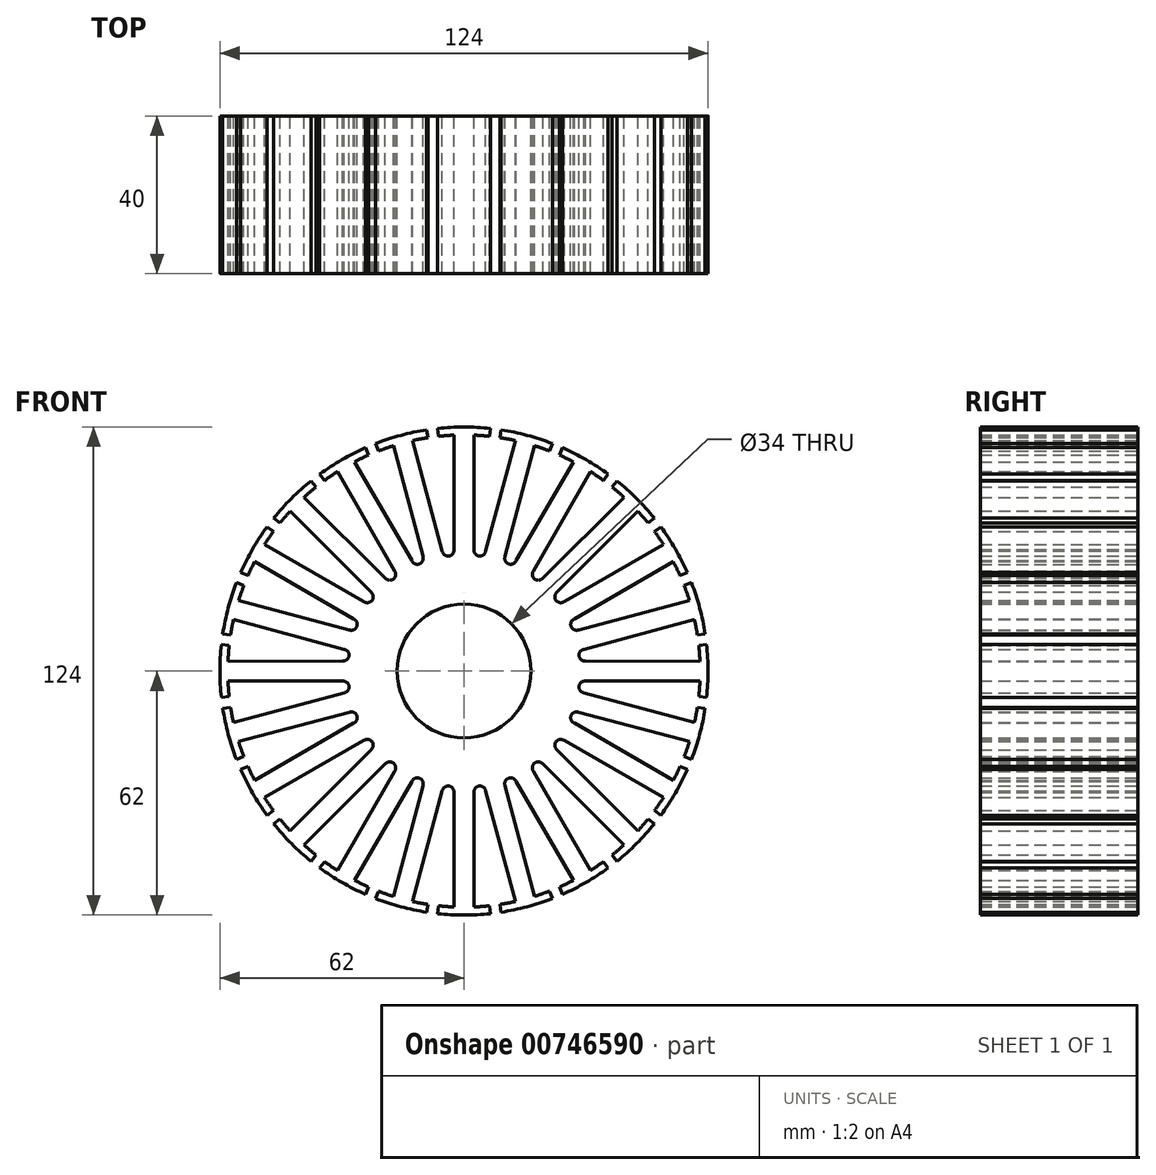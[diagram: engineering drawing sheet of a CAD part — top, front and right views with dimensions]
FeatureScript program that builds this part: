
annotation { "Feature Type Name" : "Feature", "Feature Type Description" : "" }
export const myFeature = defineFeature(function(context is Context, id is Id, definition is map)
    precondition{}
    {
        {
            var Q0;
            Q0=qCreatedBy(makeId("Front.planeOp"),FACE);
            var sketch = newSketch(context, id + "F0", { "sketchPlane" : qUnion([Q0])});
            skArc(sketch, "E0", {"start": v(6.72, 61.63) * mm, "mid": v(0, 62) * mm, "end": v(-6.72, 61.63) * mm});
            skArc(sketch, "E1", {"start": v(6.46, 59.65) * mm, "mid": v(4.48, 59.83) * mm, "end": v(2.5, 59.95) * mm});
            skCircle(sketch, "E2", {"center": v(0, 0) * mm, "radius": 17 * mm});
            skArc(sketch, "E3.trimOffspring", {"start": v(-9.2, 59.3) * mm, "mid": v(-11.16, 58.95) * mm, "end": v(-13.1, 58.55) * mm});
            skArc(sketch, "E4.trimOffspring", {"start": v(-9.46, 61.27) * mm, "mid": v(-16.05, 59.89) * mm, "end": v(-22.45, 57.8) * mm});
            skLineSegment(sketch, "E5.trimOffspring", {"start": v(6.46, 59.65) * mm, "end": v(6.72, 61.63) * mm});
            skLineSegment(sketch, "E6.trimOffspring", {"start": v(-6.46, 59.65) * mm, "end": v(-6.72, 61.63) * mm});
            skLineSegment(sketch, "E7.trimOffspring", {"start": v(-9.2, 59.3) * mm, "end": v(-9.46, 61.27) * mm});
            skLineSegment(sketch, "E8.MirrorCS", {"start": v(-21.68, 55.95) * mm, "end": v(-22.45, 57.8) * mm});
            skCircle(sketch, "E9", {"center": v(0, 0) * mm, "radius": 31 * mm, "construction": true});
            skArc(sketch, "E10", {"start": v(2.55, 30.9) * mm, "mid": v(3.85, 29.22) * mm, "end": v(5.53, 30.5) * mm});
            skArc(sketch, "E11.MirrorC", {"start": v(-2.55, 30.9) * mm, "mid": v(-3.85, 29.22) * mm, "end": v(-5.53, 30.5) * mm});
            skLineSegment(sketch, "E12.MirrorCS", {"start": v(-10.41, 29.2) * mm, "end": v(-17.93, 57.26) * mm});
            skArc(sketch, "E13.MirrorC", {"start": v(10.46, 29.18) * mm, "mid": v(11.28, 27.23) * mm, "end": v(13.24, 28.03) * mm});
            skLineSegment(sketch, "E14.trimOffspring", {"start": v(-5.58, 30.5) * mm, "end": v(-13.1, 58.55) * mm});
            skArc(sketch, "E15.MirrorCS", {"start": v(-13.24, 28.03) * mm, "mid": v(-11.28, 27.23) * mm, "end": v(-10.46, 29.18) * mm});
            skArc(sketch, "E16.trimOffspring", {"start": v(-2.5, 59.95) * mm, "mid": v(-4.48, 59.83) * mm, "end": v(-6.46, 59.65) * mm});
            skArc(sketch, "E17.trimOffspring", {"start": v(-17.93, 57.26) * mm, "mid": v(-19.82, 56.63) * mm, "end": v(-21.68, 55.95) * mm});
            skLineSegment(sketch, "E18", {"start": v(0, 0) * mm, "end": v(0, 29.47) * mm});
            skLineSegment(sketch, "E19", {"start": v(2.5, 59.95) * mm, "end": v(2.55, 30.9) * mm});
            skLineSegment(sketch, "E20", {"start": v(-2.55, 30.9) * mm, "end": v(-2.5, 59.95) * mm});
            skLineSegment(sketch, "E21.MirrorCS", {"start": v(13.1, 58.55) * mm, "end": v(5.53, 30.5) * mm});
            skLineSegment(sketch, "E22.MirrorCS", {"start": v(10.46, 29.18) * mm, "end": v(17.93, 57.26) * mm});
            skArc(sketch, "E23.MirrorCS", {"start": v(9.2, 59.3) * mm, "mid": v(11.16, 58.95) * mm, "end": v(13.1, 58.55) * mm});
            skArc(sketch, "E24.MirrorCS", {"start": v(17.93, 57.26) * mm, "mid": v(19.82, 56.63) * mm, "end": v(21.68, 55.95) * mm});
            skLineSegment(sketch, "E25.MirrorCS", {"start": v(9.2, 59.3) * mm, "end": v(9.46, 61.27) * mm});
            skLineSegment(sketch, "E26.MirrorCS", {"start": v(21.68, 55.95) * mm, "end": v(22.45, 57.8) * mm});
            skLineSegment(sketch, "E27", {"start": v(0, 0) * mm, "end": v(31, 0) * mm});
            skLineSegment(sketch, "E28.MirrorCS", {"start": v(59.76, -5.35) * mm, "end": v(30.96, -1.5) * mm});
            skLineSegment(sketch, "E29.MirrorCS", {"start": v(59.76, 5.35) * mm, "end": v(30.96, 1.5) * mm});
            skArc(sketch, "E30.MirrorCS", {"start": v(30.96, -1.5) * mm, "mid": v(29.47, 0) * mm, "end": v(30.96, 1.5) * mm});
            skLineSegment(sketch, "E31.MirrorCS", {"start": v(59.98, 1.38) * mm, "end": v(61.98, 1.38) * mm});
            skLineSegment(sketch, "E32.MirrorCS", {"start": v(59.98, -1.38) * mm, "end": v(61.98, -1.38) * mm});
            skArc(sketch, "E33.MirrorCS", {"start": v(59.98, -1.38) * mm, "mid": v(59.9, -3.36) * mm, "end": v(59.76, -5.35) * mm});
            skArc(sketch, "E34.MirrorCS", {"start": v(59.98, 1.38) * mm, "mid": v(59.9, 3.36) * mm, "end": v(59.76, 5.35) * mm});
            skArc(sketch, "E35.trimOffspring", {"start": v(22.45, 57.8) * mm, "mid": v(16.05, 59.89) * mm, "end": v(9.46, 61.27) * mm});
            skArc(sketch, "E36.trimOffspring", {"start": v(21.68, 55.95) * mm, "mid": v(19.82, 56.63) * mm, "end": v(17.93, 57.26) * mm});
            skLineSegment(sketch, "E37", {"start": v(3.85, 29.22) * mm, "end": v(0, 0) * mm});
            skLineSegment(sketch, "E38", {"start": v(-3.85, 29.22) * mm, "end": v(0, 0) * mm});
            skArc(sketch, "E39.trimOffspring", {"start": v(59.76, -5.35) * mm, "mid": v(59.9, -3.36) * mm, "end": v(59.98, -1.38) * mm});
            skCircle(sketch, "E40", {"center": v(0, 0) * mm, "radius": 29.47 * mm, "construction": true});
            skSolve(sketch);
        }
        {
            var Q0;
            Q0=makeQuery(id+"F0.imprint","IMPRINT",FACE,{"disambiguationData":[TD([[makeQuery(id+"F0.imprint","IMPRINT",EDGE,{"derivedFrom":sQuery(id+"F0.wireOp",EDGE,"E1")}),-1.0]])]});
            var Q1;
            {var subQ0=sQuery(id+"F0.wireOp",EDGE,"E6.trimOffspring");Q1=makeQuery(id+"F0.imprint","IMPRINT",FACE,{"disambiguationData":[TD([[makeQuery(id+"F0.imprint","IMPRINT",EDGE,{"derivedFrom":subQ0}),-1.0]])]});}
            var Q2;
            {var subQ0=sQuery(id+"F0.wireOp",EDGE,"E27");var subQ1=sQuery(id+"F0.wireOp",EDGE,"E2");var subQ2=makeQuery(id+"F0.imprint","INTERSECT",VERTEX,{"derivedFrom":[subQ1,subQ0]});Q2=makeQuery(id+"F0.imprint","IMPRINT",FACE,{"disambiguationData":[TD([[makeQuery(id+"F0.imprint","IMPRINT",EDGE,{"disambiguationData":[TD([[subQ2,-1.0]])],"derivedFrom":subQ1}),1.0]])]});}
            var Q3;
            {var subQ0=sQuery(id+"F0.wireOp",EDGE,"E27");var subQ1=sQuery(id+"F0.wireOp",EDGE,"E2");var subQ2=makeQuery(id+"F0.imprint","INTERSECT",VERTEX,{"derivedFrom":[subQ1,subQ0]});Q3=makeQuery(id+"F0.imprint","IMPRINT",FACE,{"disambiguationData":[TD([[makeQuery(id+"F0.imprint","IMPRINT",EDGE,{"disambiguationData":[TD([[subQ2,1.0]])],"derivedFrom":subQ1}),1.0]])]});}
            var Q4;
            {var subQ0=sQuery(id+"F0.wireOp",EDGE,"E38");var subQ1=sQuery(id+"F0.wireOp",EDGE,"E2");var subQ2=makeQuery(id+"F0.imprint","INTERSECT",VERTEX,{"derivedFrom":[subQ1,subQ0]});Q4=makeQuery(id+"F0.imprint","IMPRINT",FACE,{"disambiguationData":[TD([[makeQuery(id+"F0.imprint","IMPRINT",EDGE,{"disambiguationData":[TD([[subQ2,1.0]])],"derivedFrom":subQ1}),1.0]])]});}
            var Q5;
            {var subQ0=sQuery(id+"F0.wireOp",EDGE,"E37");var subQ1=sQuery(id+"F0.wireOp",EDGE,"E2");var subQ2=makeQuery(id+"F0.imprint","INTERSECT",VERTEX,{"derivedFrom":[subQ1,subQ0]});Q5=makeQuery(id+"F0.imprint","IMPRINT",FACE,{"disambiguationData":[TD([[makeQuery(id+"F0.imprint","IMPRINT",EDGE,{"disambiguationData":[TD([[subQ2,-1.0]])],"derivedFrom":subQ1}),1.0]])]});}
            extrude(context, id + "F1", {"entities" : qUnion([Q0, Q1, Q2, Q3, Q4, Q5]), "depth" : 40 * mm, "offsetDistance" : 25 * mm});
        }
        {
            var Q0;
            Q0=makeQuery(id+"F1.opExtrude","SWEPT_BODY",BODY,{"disambiguationData":[OSD([sQuery(id+"F0.wireOp",EDGE,"E0"),sQuery(id+"F0.wireOp",EDGE,"E1"),sQuery(id+"F0.wireOp",EDGE,"E2"),sQuery(id+"F0.wireOp",EDGE,"E5.trimOffspring"),sQuery(id+"F0.wireOp",EDGE,"E6.trimOffspring"),sQuery(id+"F0.wireOp",EDGE,"E10"),sQuery(id+"F0.wireOp",EDGE,"E11.MirrorC"),sQuery(id+"F0.wireOp",EDGE,"E16.trimOffspring"),sQuery(id+"F0.wireOp",EDGE,"E19"),sQuery(id+"F0.wireOp",EDGE,"E20"),sQuery(id+"F0.wireOp",EDGE,"E37"),sQuery(id+"F0.wireOp",EDGE,"E38")])]});
            var Q1;
            Q1=makeQuery(id+"F1.opExtrude","SWEPT_FACE",FACE,{"disambiguationData":[OSD([sQuery(id+"F0.wireOp",EDGE,"E2")])]});
            circularPattern(context, id + "F2", {"entities" : qUnion([Q0]), "axis" : qUnion([Q1]), "angle" : 360 * degree, "instanceCount" : 24, "equalSpace" : true});
        }
        {
            var Q0;
            Q0=makeQuery(id+"F1.opExtrude","SWEPT_BODY",BODY,{"disambiguationData":[OSD([sQuery(id+"F0.wireOp",EDGE,"E0"),sQuery(id+"F0.wireOp",EDGE,"E1"),sQuery(id+"F0.wireOp",EDGE,"E2"),sQuery(id+"F0.wireOp",EDGE,"E5.trimOffspring"),sQuery(id+"F0.wireOp",EDGE,"E6.trimOffspring"),sQuery(id+"F0.wireOp",EDGE,"E10"),sQuery(id+"F0.wireOp",EDGE,"E11.MirrorC"),sQuery(id+"F0.wireOp",EDGE,"E16.trimOffspring"),sQuery(id+"F0.wireOp",EDGE,"E19"),sQuery(id+"F0.wireOp",EDGE,"E20"),sQuery(id+"F0.wireOp",EDGE,"E37"),sQuery(id+"F0.wireOp",EDGE,"E38")])]});
            var Q1;
            Q1=makeQuery(id+"F2.opPattern","COPY",BODY,{"derivedFrom":makeQuery(id+"F1.opExtrude","SWEPT_BODY",BODY,{"disambiguationData":[OSD([sQuery(id+"F0.wireOp",EDGE,"E0"),sQuery(id+"F0.wireOp",EDGE,"E1"),sQuery(id+"F0.wireOp",EDGE,"E2"),sQuery(id+"F0.wireOp",EDGE,"E5.trimOffspring"),sQuery(id+"F0.wireOp",EDGE,"E6.trimOffspring"),sQuery(id+"F0.wireOp",EDGE,"E10"),sQuery(id+"F0.wireOp",EDGE,"E11.MirrorC"),sQuery(id+"F0.wireOp",EDGE,"E16.trimOffspring"),sQuery(id+"F0.wireOp",EDGE,"E19"),sQuery(id+"F0.wireOp",EDGE,"E20"),sQuery(id+"F0.wireOp",EDGE,"E37"),sQuery(id+"F0.wireOp",EDGE,"E38")])]}),"instanceName":"4"});
            var Q2;
            Q2=makeQuery(id+"F2.opPattern","COPY",BODY,{"derivedFrom":makeQuery(id+"F1.opExtrude","SWEPT_BODY",BODY,{"disambiguationData":[OSD([sQuery(id+"F0.wireOp",EDGE,"E0"),sQuery(id+"F0.wireOp",EDGE,"E1"),sQuery(id+"F0.wireOp",EDGE,"E2"),sQuery(id+"F0.wireOp",EDGE,"E5.trimOffspring"),sQuery(id+"F0.wireOp",EDGE,"E6.trimOffspring"),sQuery(id+"F0.wireOp",EDGE,"E10"),sQuery(id+"F0.wireOp",EDGE,"E11.MirrorC"),sQuery(id+"F0.wireOp",EDGE,"E16.trimOffspring"),sQuery(id+"F0.wireOp",EDGE,"E19"),sQuery(id+"F0.wireOp",EDGE,"E20"),sQuery(id+"F0.wireOp",EDGE,"E37"),sQuery(id+"F0.wireOp",EDGE,"E38")])]}),"instanceName":"3"});
            var Q3;
            Q3=makeQuery(id+"F2.opPattern","COPY",BODY,{"derivedFrom":makeQuery(id+"F1.opExtrude","SWEPT_BODY",BODY,{"disambiguationData":[OSD([sQuery(id+"F0.wireOp",EDGE,"E0"),sQuery(id+"F0.wireOp",EDGE,"E1"),sQuery(id+"F0.wireOp",EDGE,"E2"),sQuery(id+"F0.wireOp",EDGE,"E5.trimOffspring"),sQuery(id+"F0.wireOp",EDGE,"E6.trimOffspring"),sQuery(id+"F0.wireOp",EDGE,"E10"),sQuery(id+"F0.wireOp",EDGE,"E11.MirrorC"),sQuery(id+"F0.wireOp",EDGE,"E16.trimOffspring"),sQuery(id+"F0.wireOp",EDGE,"E19"),sQuery(id+"F0.wireOp",EDGE,"E20"),sQuery(id+"F0.wireOp",EDGE,"E37"),sQuery(id+"F0.wireOp",EDGE,"E38")])]}),"instanceName":"7"});
            var Q4;
            Q4=makeQuery(id+"F2.opPattern","COPY",BODY,{"derivedFrom":makeQuery(id+"F1.opExtrude","SWEPT_BODY",BODY,{"disambiguationData":[OSD([sQuery(id+"F0.wireOp",EDGE,"E0"),sQuery(id+"F0.wireOp",EDGE,"E1"),sQuery(id+"F0.wireOp",EDGE,"E2"),sQuery(id+"F0.wireOp",EDGE,"E5.trimOffspring"),sQuery(id+"F0.wireOp",EDGE,"E6.trimOffspring"),sQuery(id+"F0.wireOp",EDGE,"E10"),sQuery(id+"F0.wireOp",EDGE,"E11.MirrorC"),sQuery(id+"F0.wireOp",EDGE,"E16.trimOffspring"),sQuery(id+"F0.wireOp",EDGE,"E19"),sQuery(id+"F0.wireOp",EDGE,"E20"),sQuery(id+"F0.wireOp",EDGE,"E37"),sQuery(id+"F0.wireOp",EDGE,"E38")])]}),"instanceName":"5"});
            var Q5;
            Q5=makeQuery(id+"F2.opPattern","COPY",BODY,{"derivedFrom":makeQuery(id+"F1.opExtrude","SWEPT_BODY",BODY,{"disambiguationData":[OSD([sQuery(id+"F0.wireOp",EDGE,"E0"),sQuery(id+"F0.wireOp",EDGE,"E1"),sQuery(id+"F0.wireOp",EDGE,"E2"),sQuery(id+"F0.wireOp",EDGE,"E5.trimOffspring"),sQuery(id+"F0.wireOp",EDGE,"E6.trimOffspring"),sQuery(id+"F0.wireOp",EDGE,"E10"),sQuery(id+"F0.wireOp",EDGE,"E11.MirrorC"),sQuery(id+"F0.wireOp",EDGE,"E16.trimOffspring"),sQuery(id+"F0.wireOp",EDGE,"E19"),sQuery(id+"F0.wireOp",EDGE,"E20"),sQuery(id+"F0.wireOp",EDGE,"E37"),sQuery(id+"F0.wireOp",EDGE,"E38")])]}),"instanceName":"2"});
            var Q6;
            Q6=makeQuery(id+"F2.opPattern","COPY",BODY,{"derivedFrom":makeQuery(id+"F1.opExtrude","SWEPT_BODY",BODY,{"disambiguationData":[OSD([sQuery(id+"F0.wireOp",EDGE,"E0"),sQuery(id+"F0.wireOp",EDGE,"E1"),sQuery(id+"F0.wireOp",EDGE,"E2"),sQuery(id+"F0.wireOp",EDGE,"E5.trimOffspring"),sQuery(id+"F0.wireOp",EDGE,"E6.trimOffspring"),sQuery(id+"F0.wireOp",EDGE,"E10"),sQuery(id+"F0.wireOp",EDGE,"E11.MirrorC"),sQuery(id+"F0.wireOp",EDGE,"E16.trimOffspring"),sQuery(id+"F0.wireOp",EDGE,"E19"),sQuery(id+"F0.wireOp",EDGE,"E20"),sQuery(id+"F0.wireOp",EDGE,"E37"),sQuery(id+"F0.wireOp",EDGE,"E38")])]}),"instanceName":"1"});
            var Q7;
            Q7=makeQuery(id+"F2.opPattern","COPY",BODY,{"derivedFrom":makeQuery(id+"F1.opExtrude","SWEPT_BODY",BODY,{"disambiguationData":[OSD([sQuery(id+"F0.wireOp",EDGE,"E0"),sQuery(id+"F0.wireOp",EDGE,"E1"),sQuery(id+"F0.wireOp",EDGE,"E2"),sQuery(id+"F0.wireOp",EDGE,"E5.trimOffspring"),sQuery(id+"F0.wireOp",EDGE,"E6.trimOffspring"),sQuery(id+"F0.wireOp",EDGE,"E10"),sQuery(id+"F0.wireOp",EDGE,"E11.MirrorC"),sQuery(id+"F0.wireOp",EDGE,"E16.trimOffspring"),sQuery(id+"F0.wireOp",EDGE,"E19"),sQuery(id+"F0.wireOp",EDGE,"E20"),sQuery(id+"F0.wireOp",EDGE,"E37"),sQuery(id+"F0.wireOp",EDGE,"E38")])]}),"instanceName":"9"});
            var Q8;
            Q8=makeQuery(id+"F2.opPattern","COPY",BODY,{"derivedFrom":makeQuery(id+"F1.opExtrude","SWEPT_BODY",BODY,{"disambiguationData":[OSD([sQuery(id+"F0.wireOp",EDGE,"E0"),sQuery(id+"F0.wireOp",EDGE,"E1"),sQuery(id+"F0.wireOp",EDGE,"E2"),sQuery(id+"F0.wireOp",EDGE,"E5.trimOffspring"),sQuery(id+"F0.wireOp",EDGE,"E6.trimOffspring"),sQuery(id+"F0.wireOp",EDGE,"E10"),sQuery(id+"F0.wireOp",EDGE,"E11.MirrorC"),sQuery(id+"F0.wireOp",EDGE,"E16.trimOffspring"),sQuery(id+"F0.wireOp",EDGE,"E19"),sQuery(id+"F0.wireOp",EDGE,"E20"),sQuery(id+"F0.wireOp",EDGE,"E37"),sQuery(id+"F0.wireOp",EDGE,"E38")])]}),"instanceName":"8"});
            var Q9;
            Q9=makeQuery(id+"F2.opPattern","COPY",BODY,{"derivedFrom":makeQuery(id+"F1.opExtrude","SWEPT_BODY",BODY,{"disambiguationData":[OSD([sQuery(id+"F0.wireOp",EDGE,"E0"),sQuery(id+"F0.wireOp",EDGE,"E1"),sQuery(id+"F0.wireOp",EDGE,"E2"),sQuery(id+"F0.wireOp",EDGE,"E5.trimOffspring"),sQuery(id+"F0.wireOp",EDGE,"E6.trimOffspring"),sQuery(id+"F0.wireOp",EDGE,"E10"),sQuery(id+"F0.wireOp",EDGE,"E11.MirrorC"),sQuery(id+"F0.wireOp",EDGE,"E16.trimOffspring"),sQuery(id+"F0.wireOp",EDGE,"E19"),sQuery(id+"F0.wireOp",EDGE,"E20"),sQuery(id+"F0.wireOp",EDGE,"E37"),sQuery(id+"F0.wireOp",EDGE,"E38")])]}),"instanceName":"6"});
            var Q10;
            Q10=makeQuery(id+"F2.opPattern","COPY",BODY,{"derivedFrom":makeQuery(id+"F1.opExtrude","SWEPT_BODY",BODY,{"disambiguationData":[OSD([sQuery(id+"F0.wireOp",EDGE,"E0"),sQuery(id+"F0.wireOp",EDGE,"E1"),sQuery(id+"F0.wireOp",EDGE,"E2"),sQuery(id+"F0.wireOp",EDGE,"E5.trimOffspring"),sQuery(id+"F0.wireOp",EDGE,"E6.trimOffspring"),sQuery(id+"F0.wireOp",EDGE,"E10"),sQuery(id+"F0.wireOp",EDGE,"E11.MirrorC"),sQuery(id+"F0.wireOp",EDGE,"E16.trimOffspring"),sQuery(id+"F0.wireOp",EDGE,"E19"),sQuery(id+"F0.wireOp",EDGE,"E20"),sQuery(id+"F0.wireOp",EDGE,"E37"),sQuery(id+"F0.wireOp",EDGE,"E38")])]}),"instanceName":"13"});
            var Q11;
            Q11=makeQuery(id+"F2.opPattern","COPY",BODY,{"derivedFrom":makeQuery(id+"F1.opExtrude","SWEPT_BODY",BODY,{"disambiguationData":[OSD([sQuery(id+"F0.wireOp",EDGE,"E0"),sQuery(id+"F0.wireOp",EDGE,"E1"),sQuery(id+"F0.wireOp",EDGE,"E2"),sQuery(id+"F0.wireOp",EDGE,"E5.trimOffspring"),sQuery(id+"F0.wireOp",EDGE,"E6.trimOffspring"),sQuery(id+"F0.wireOp",EDGE,"E10"),sQuery(id+"F0.wireOp",EDGE,"E11.MirrorC"),sQuery(id+"F0.wireOp",EDGE,"E16.trimOffspring"),sQuery(id+"F0.wireOp",EDGE,"E19"),sQuery(id+"F0.wireOp",EDGE,"E20"),sQuery(id+"F0.wireOp",EDGE,"E37"),sQuery(id+"F0.wireOp",EDGE,"E38")])]}),"instanceName":"12"});
            var Q12;
            Q12=makeQuery(id+"F2.opPattern","COPY",BODY,{"derivedFrom":makeQuery(id+"F1.opExtrude","SWEPT_BODY",BODY,{"disambiguationData":[OSD([sQuery(id+"F0.wireOp",EDGE,"E0"),sQuery(id+"F0.wireOp",EDGE,"E1"),sQuery(id+"F0.wireOp",EDGE,"E2"),sQuery(id+"F0.wireOp",EDGE,"E5.trimOffspring"),sQuery(id+"F0.wireOp",EDGE,"E6.trimOffspring"),sQuery(id+"F0.wireOp",EDGE,"E10"),sQuery(id+"F0.wireOp",EDGE,"E11.MirrorC"),sQuery(id+"F0.wireOp",EDGE,"E16.trimOffspring"),sQuery(id+"F0.wireOp",EDGE,"E19"),sQuery(id+"F0.wireOp",EDGE,"E20"),sQuery(id+"F0.wireOp",EDGE,"E37"),sQuery(id+"F0.wireOp",EDGE,"E38")])]}),"instanceName":"11"});
            var Q13;
            Q13=makeQuery(id+"F2.opPattern","COPY",BODY,{"derivedFrom":makeQuery(id+"F1.opExtrude","SWEPT_BODY",BODY,{"disambiguationData":[OSD([sQuery(id+"F0.wireOp",EDGE,"E0"),sQuery(id+"F0.wireOp",EDGE,"E1"),sQuery(id+"F0.wireOp",EDGE,"E2"),sQuery(id+"F0.wireOp",EDGE,"E5.trimOffspring"),sQuery(id+"F0.wireOp",EDGE,"E6.trimOffspring"),sQuery(id+"F0.wireOp",EDGE,"E10"),sQuery(id+"F0.wireOp",EDGE,"E11.MirrorC"),sQuery(id+"F0.wireOp",EDGE,"E16.trimOffspring"),sQuery(id+"F0.wireOp",EDGE,"E19"),sQuery(id+"F0.wireOp",EDGE,"E20"),sQuery(id+"F0.wireOp",EDGE,"E37"),sQuery(id+"F0.wireOp",EDGE,"E38")])]}),"instanceName":"10"});
            var Q14;
            Q14=makeQuery(id+"F2.opPattern","COPY",BODY,{"derivedFrom":makeQuery(id+"F1.opExtrude","SWEPT_BODY",BODY,{"disambiguationData":[OSD([sQuery(id+"F0.wireOp",EDGE,"E0"),sQuery(id+"F0.wireOp",EDGE,"E1"),sQuery(id+"F0.wireOp",EDGE,"E2"),sQuery(id+"F0.wireOp",EDGE,"E5.trimOffspring"),sQuery(id+"F0.wireOp",EDGE,"E6.trimOffspring"),sQuery(id+"F0.wireOp",EDGE,"E10"),sQuery(id+"F0.wireOp",EDGE,"E11.MirrorC"),sQuery(id+"F0.wireOp",EDGE,"E16.trimOffspring"),sQuery(id+"F0.wireOp",EDGE,"E19"),sQuery(id+"F0.wireOp",EDGE,"E20"),sQuery(id+"F0.wireOp",EDGE,"E37"),sQuery(id+"F0.wireOp",EDGE,"E38")])]}),"instanceName":"17"});
            var Q15;
            Q15=makeQuery(id+"F2.opPattern","COPY",BODY,{"derivedFrom":makeQuery(id+"F1.opExtrude","SWEPT_BODY",BODY,{"disambiguationData":[OSD([sQuery(id+"F0.wireOp",EDGE,"E0"),sQuery(id+"F0.wireOp",EDGE,"E1"),sQuery(id+"F0.wireOp",EDGE,"E2"),sQuery(id+"F0.wireOp",EDGE,"E5.trimOffspring"),sQuery(id+"F0.wireOp",EDGE,"E6.trimOffspring"),sQuery(id+"F0.wireOp",EDGE,"E10"),sQuery(id+"F0.wireOp",EDGE,"E11.MirrorC"),sQuery(id+"F0.wireOp",EDGE,"E16.trimOffspring"),sQuery(id+"F0.wireOp",EDGE,"E19"),sQuery(id+"F0.wireOp",EDGE,"E20"),sQuery(id+"F0.wireOp",EDGE,"E37"),sQuery(id+"F0.wireOp",EDGE,"E38")])]}),"instanceName":"16"});
            var Q16;
            Q16=makeQuery(id+"F2.opPattern","COPY",BODY,{"derivedFrom":makeQuery(id+"F1.opExtrude","SWEPT_BODY",BODY,{"disambiguationData":[OSD([sQuery(id+"F0.wireOp",EDGE,"E0"),sQuery(id+"F0.wireOp",EDGE,"E1"),sQuery(id+"F0.wireOp",EDGE,"E2"),sQuery(id+"F0.wireOp",EDGE,"E5.trimOffspring"),sQuery(id+"F0.wireOp",EDGE,"E6.trimOffspring"),sQuery(id+"F0.wireOp",EDGE,"E10"),sQuery(id+"F0.wireOp",EDGE,"E11.MirrorC"),sQuery(id+"F0.wireOp",EDGE,"E16.trimOffspring"),sQuery(id+"F0.wireOp",EDGE,"E19"),sQuery(id+"F0.wireOp",EDGE,"E20"),sQuery(id+"F0.wireOp",EDGE,"E37"),sQuery(id+"F0.wireOp",EDGE,"E38")])]}),"instanceName":"15"});
            var Q17;
            Q17=makeQuery(id+"F2.opPattern","COPY",BODY,{"derivedFrom":makeQuery(id+"F1.opExtrude","SWEPT_BODY",BODY,{"disambiguationData":[OSD([sQuery(id+"F0.wireOp",EDGE,"E0"),sQuery(id+"F0.wireOp",EDGE,"E1"),sQuery(id+"F0.wireOp",EDGE,"E2"),sQuery(id+"F0.wireOp",EDGE,"E5.trimOffspring"),sQuery(id+"F0.wireOp",EDGE,"E6.trimOffspring"),sQuery(id+"F0.wireOp",EDGE,"E10"),sQuery(id+"F0.wireOp",EDGE,"E11.MirrorC"),sQuery(id+"F0.wireOp",EDGE,"E16.trimOffspring"),sQuery(id+"F0.wireOp",EDGE,"E19"),sQuery(id+"F0.wireOp",EDGE,"E20"),sQuery(id+"F0.wireOp",EDGE,"E37"),sQuery(id+"F0.wireOp",EDGE,"E38")])]}),"instanceName":"14"});
            var Q18;
            Q18=makeQuery(id+"F2.opPattern","COPY",BODY,{"derivedFrom":makeQuery(id+"F1.opExtrude","SWEPT_BODY",BODY,{"disambiguationData":[OSD([sQuery(id+"F0.wireOp",EDGE,"E0"),sQuery(id+"F0.wireOp",EDGE,"E1"),sQuery(id+"F0.wireOp",EDGE,"E2"),sQuery(id+"F0.wireOp",EDGE,"E5.trimOffspring"),sQuery(id+"F0.wireOp",EDGE,"E6.trimOffspring"),sQuery(id+"F0.wireOp",EDGE,"E10"),sQuery(id+"F0.wireOp",EDGE,"E11.MirrorC"),sQuery(id+"F0.wireOp",EDGE,"E16.trimOffspring"),sQuery(id+"F0.wireOp",EDGE,"E19"),sQuery(id+"F0.wireOp",EDGE,"E20"),sQuery(id+"F0.wireOp",EDGE,"E37"),sQuery(id+"F0.wireOp",EDGE,"E38")])]}),"instanceName":"21"});
            var Q19;
            Q19=makeQuery(id+"F2.opPattern","COPY",BODY,{"derivedFrom":makeQuery(id+"F1.opExtrude","SWEPT_BODY",BODY,{"disambiguationData":[OSD([sQuery(id+"F0.wireOp",EDGE,"E0"),sQuery(id+"F0.wireOp",EDGE,"E1"),sQuery(id+"F0.wireOp",EDGE,"E2"),sQuery(id+"F0.wireOp",EDGE,"E5.trimOffspring"),sQuery(id+"F0.wireOp",EDGE,"E6.trimOffspring"),sQuery(id+"F0.wireOp",EDGE,"E10"),sQuery(id+"F0.wireOp",EDGE,"E11.MirrorC"),sQuery(id+"F0.wireOp",EDGE,"E16.trimOffspring"),sQuery(id+"F0.wireOp",EDGE,"E19"),sQuery(id+"F0.wireOp",EDGE,"E20"),sQuery(id+"F0.wireOp",EDGE,"E37"),sQuery(id+"F0.wireOp",EDGE,"E38")])]}),"instanceName":"20"});
            var Q20;
            Q20=makeQuery(id+"F2.opPattern","COPY",BODY,{"derivedFrom":makeQuery(id+"F1.opExtrude","SWEPT_BODY",BODY,{"disambiguationData":[OSD([sQuery(id+"F0.wireOp",EDGE,"E0"),sQuery(id+"F0.wireOp",EDGE,"E1"),sQuery(id+"F0.wireOp",EDGE,"E2"),sQuery(id+"F0.wireOp",EDGE,"E5.trimOffspring"),sQuery(id+"F0.wireOp",EDGE,"E6.trimOffspring"),sQuery(id+"F0.wireOp",EDGE,"E10"),sQuery(id+"F0.wireOp",EDGE,"E11.MirrorC"),sQuery(id+"F0.wireOp",EDGE,"E16.trimOffspring"),sQuery(id+"F0.wireOp",EDGE,"E19"),sQuery(id+"F0.wireOp",EDGE,"E20"),sQuery(id+"F0.wireOp",EDGE,"E37"),sQuery(id+"F0.wireOp",EDGE,"E38")])]}),"instanceName":"19"});
            var Q21;
            Q21=makeQuery(id+"F2.opPattern","COPY",BODY,{"derivedFrom":makeQuery(id+"F1.opExtrude","SWEPT_BODY",BODY,{"disambiguationData":[OSD([sQuery(id+"F0.wireOp",EDGE,"E0"),sQuery(id+"F0.wireOp",EDGE,"E1"),sQuery(id+"F0.wireOp",EDGE,"E2"),sQuery(id+"F0.wireOp",EDGE,"E5.trimOffspring"),sQuery(id+"F0.wireOp",EDGE,"E6.trimOffspring"),sQuery(id+"F0.wireOp",EDGE,"E10"),sQuery(id+"F0.wireOp",EDGE,"E11.MirrorC"),sQuery(id+"F0.wireOp",EDGE,"E16.trimOffspring"),sQuery(id+"F0.wireOp",EDGE,"E19"),sQuery(id+"F0.wireOp",EDGE,"E20"),sQuery(id+"F0.wireOp",EDGE,"E37"),sQuery(id+"F0.wireOp",EDGE,"E38")])]}),"instanceName":"18"});
            var Q22;
            Q22=makeQuery(id+"F2.opPattern","COPY",BODY,{"derivedFrom":makeQuery(id+"F1.opExtrude","SWEPT_BODY",BODY,{"disambiguationData":[OSD([sQuery(id+"F0.wireOp",EDGE,"E0"),sQuery(id+"F0.wireOp",EDGE,"E1"),sQuery(id+"F0.wireOp",EDGE,"E2"),sQuery(id+"F0.wireOp",EDGE,"E5.trimOffspring"),sQuery(id+"F0.wireOp",EDGE,"E6.trimOffspring"),sQuery(id+"F0.wireOp",EDGE,"E10"),sQuery(id+"F0.wireOp",EDGE,"E11.MirrorC"),sQuery(id+"F0.wireOp",EDGE,"E16.trimOffspring"),sQuery(id+"F0.wireOp",EDGE,"E19"),sQuery(id+"F0.wireOp",EDGE,"E20"),sQuery(id+"F0.wireOp",EDGE,"E37"),sQuery(id+"F0.wireOp",EDGE,"E38")])]}),"instanceName":"22"});
            var Q23;
            Q23=makeQuery(id+"F2.opPattern","COPY",BODY,{"derivedFrom":makeQuery(id+"F1.opExtrude","SWEPT_BODY",BODY,{"disambiguationData":[OSD([sQuery(id+"F0.wireOp",EDGE,"E0"),sQuery(id+"F0.wireOp",EDGE,"E1"),sQuery(id+"F0.wireOp",EDGE,"E2"),sQuery(id+"F0.wireOp",EDGE,"E5.trimOffspring"),sQuery(id+"F0.wireOp",EDGE,"E6.trimOffspring"),sQuery(id+"F0.wireOp",EDGE,"E10"),sQuery(id+"F0.wireOp",EDGE,"E11.MirrorC"),sQuery(id+"F0.wireOp",EDGE,"E16.trimOffspring"),sQuery(id+"F0.wireOp",EDGE,"E19"),sQuery(id+"F0.wireOp",EDGE,"E20"),sQuery(id+"F0.wireOp",EDGE,"E37"),sQuery(id+"F0.wireOp",EDGE,"E38")])]}),"instanceName":"23"});
            booleanBodies(context, id + "F3", {"operationType" : BooleanOperationType.UNION, "tools" : qUnion([Q0, Q1, Q2, Q3, Q4, Q5, Q6, Q7, Q8, Q9, Q10, Q11, Q12, Q13, Q14, Q15, Q16, Q17, Q18, Q19, Q20, Q21, Q22, Q23])});
        }
        {
            var Q0;
            {var subQ0=sQuery(id+"F0.wireOp",EDGE,"E27");var subQ1=sQuery(id+"F0.wireOp",EDGE,"E2");var subQ2=makeQuery(id+"F0.imprint","INTERSECT",VERTEX,{"derivedFrom":[subQ1,subQ0]});Q0=makeQuery(id+"F0.imprint","IMPRINT",FACE,{"disambiguationData":[TD([[makeQuery(id+"F0.imprint","IMPRINT",EDGE,{"disambiguationData":[TD([[subQ2,1.0]])],"derivedFrom":subQ1}),1.0]])]});}
            var Q1;
            {var subQ0=sQuery(id+"F0.wireOp",EDGE,"E27");var subQ1=sQuery(id+"F0.wireOp",EDGE,"E2");var subQ2=makeQuery(id+"F0.imprint","INTERSECT",VERTEX,{"derivedFrom":[subQ1,subQ0]});Q1=makeQuery(id+"F0.imprint","IMPRINT",FACE,{"disambiguationData":[TD([[makeQuery(id+"F0.imprint","IMPRINT",EDGE,{"disambiguationData":[TD([[subQ2,-1.0]])],"derivedFrom":subQ1}),1.0]])]});}
            var Q2;
            {var subQ0=sQuery(id+"F0.wireOp",EDGE,"E37");var subQ1=sQuery(id+"F0.wireOp",EDGE,"E2");var subQ2=makeQuery(id+"F0.imprint","INTERSECT",VERTEX,{"derivedFrom":[subQ1,subQ0]});Q2=makeQuery(id+"F0.imprint","IMPRINT",FACE,{"disambiguationData":[TD([[makeQuery(id+"F0.imprint","IMPRINT",EDGE,{"disambiguationData":[TD([[subQ2,-1.0]])],"derivedFrom":subQ1}),1.0]])]});}
            var Q3;
            {var subQ0=sQuery(id+"F0.wireOp",EDGE,"E38");var subQ1=sQuery(id+"F0.wireOp",EDGE,"E2");var subQ2=makeQuery(id+"F0.imprint","INTERSECT",VERTEX,{"derivedFrom":[subQ1,subQ0]});Q3=makeQuery(id+"F0.imprint","IMPRINT",FACE,{"disambiguationData":[TD([[makeQuery(id+"F0.imprint","IMPRINT",EDGE,{"disambiguationData":[TD([[subQ2,1.0]])],"derivedFrom":subQ1}),1.0]])]});}
            extrude(context, id + "F4", {"entities" : qUnion([Q0, Q1, Q2, Q3]), "operationType" : NewBodyOperationType.REMOVE, "depth" : 130.6 * mm, "offsetDistance" : 25 * mm});
        }
    });
